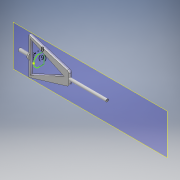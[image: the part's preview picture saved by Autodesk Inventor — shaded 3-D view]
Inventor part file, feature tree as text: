
AUTODESK INVENTOR PART (.ipt)
format: ipt  version: 2018 (Build 220112000, 112)  size: 228,352 bytes
history: native  units: mm
features: sketch x12, extrude x11, fillet x2, plane x1, projected_geometry x1
ambient origin geometry x8: Origin, YZ Plane, XZ Plane, XY Plane, X Axis, Y Axis, Z Axis, Center Point
bodies: Solid1 (feature_tree)
feature tree (27):
  extrude  "Extrusion1"  Depth=10.0mm TaperAngle=0.0deg
  sketch  "Sketch2"  dims[d3=9.0mm d4=8.0mm d5=10.0mm d6=0.0mm]
  extrude  "Extrusion2"  Depth=10.0mm TaperAngle=0.0deg
  extrude  "Extrusion3"  Depth=1.125mm
  extrude  "Extrusion4"  Depth=1.6mm
  extrude  "Extrusion5"  Depth=1.8mm
  extrude  "Extrusion6"  Depth=2.4mm
  extrude  "Extrusion7"  Depth=3.32mm
  extrude  "Extrusion8"  Depth=10.0mm
  extrude  "Extrusion9"  Depth=15.0mm TaperAngle=0.0deg
  plane  "Work Plane1"
  extrude  "Extrusion11"  Depth=1.175mm
  extrude  "Extrusion13"  Depth=10.0mm TaperAngle=0.0deg
  fillet  "Fillet1"  Radius=8.0mm
  fillet  "Fillet2"  Radius=4.1mm
  sketch  "Sketch1"  dims[d0=10.0mm d1=10.0mm d2=0.0mm]
  sketch  "Sketch3"  dims[d9=1.125mm d10=1.125mm]
  sketch  "Sketch4"  dims[d12=0.0mm d13=0.0mm d16=1.6mm]
  sketch  "Sketch5"  dims[d18=1.6mm d21=1.8mm]
  projected_geometry  "Projected Loop1"
  sketch  "Sketch6"  dims[d23=1.8mm d24=2.4mm]
  sketch  "Sketch7"  dims[d26=3.32mm d27=3.32mm]
  sketch  "Sketch8"  dims[d29=10.0mm d30=0.0mm d31=5.0mm]
  sketch  "Sketch9"  dims[d32=2.4mm d33=15.0mm d34=0.0mm]
  sketch  "Sketch10"  dims[d35=15.0mm d36=0.0mm d37=1.175mm]
  sketch  "Sketch12"  dims[d38=7.0mm d39=0.0mm d40=10.0mm d41=0.0mm d42=8.0mm d43=0.0mm d60=4.1mm]
  sketch  "Sketch13"  dims[d61=25.4mm d62=29.4mm d63=14.7mm d64=10.0mm d65=2.18mm d66=0.0mm d67=31.0mm d69=2.5mm d70=0.78mm d71=1.7mm d74=2.18mm d75=30.0mm d76=0.0mm d77=2.0mm d78=2.0mm]
